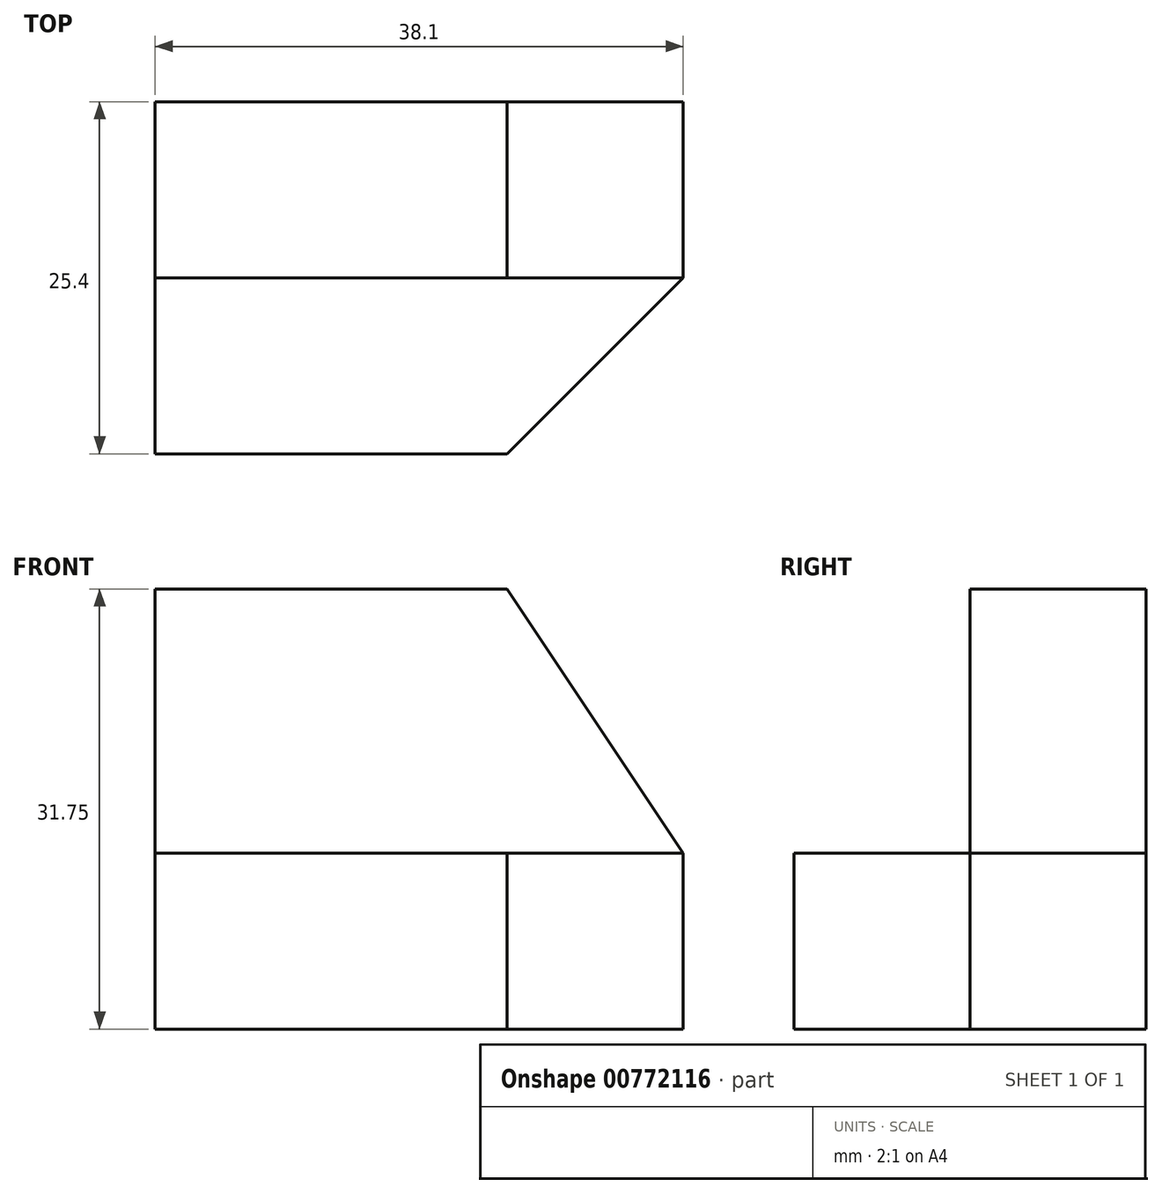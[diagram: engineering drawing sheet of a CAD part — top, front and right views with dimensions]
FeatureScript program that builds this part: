
annotation { "Feature Type Name" : "Feature", "Feature Type Description" : "" }
export const myFeature = defineFeature(function(context is Context, id is Id, definition is map)
    precondition{}
    {
        {
            var Q0;
            Q0=qCreatedBy(makeId("Right.planeOp"),FACE);
            var sketch = newSketch(context, id + "F0", { "sketchPlane" : qUnion([Q0])});
            skLineSegment(sketch, "E0", {"start": v(0, 0) * mm, "end": v(0, 31.75) * mm});
            skLineSegment(sketch, "E1", {"start": v(0, 31.75) * mm, "end": v(-12.7, 31.75) * mm});
            skLineSegment(sketch, "E2", {"start": v(-12.7, 31.75) * mm, "end": v(-12.7, 12.7) * mm});
            skLineSegment(sketch, "E3", {"start": v(-12.7, 12.7) * mm, "end": v(-25.4, 12.7) * mm});
            skLineSegment(sketch, "E4", {"start": v(-25.4, 12.7) * mm, "end": v(-25.4, 0) * mm});
            skLineSegment(sketch, "E5", {"start": v(-25.4, 0) * mm, "end": v(0, 0) * mm});
            skSolve(sketch);
        }
        {
            var Q0;
            Q0 = qSketchRegion(id + "F0", true);
            extrude(context, id + "F1", {"entities" : qUnion([Q0]), "depth" : 38.1 * mm, "offsetDistance" : 25.4 * mm});
        }
        {
            var Q0;
            Q0=makeQuery(id+"F1.opExtrude","SWEPT_FACE",FACE,{"disambiguationData":[OSD([sQuery(id+"F0.wireOp",EDGE,"E2")])]});
            var sketch = newSketch(context, id + "F2", { "sketchPlane" : qUnion([Q0])});
            skLineSegment(sketch, "E6", {"start": v(0, 31.75) * mm, "end": v(25.4, 31.75) * mm});
            skLineSegment(sketch, "E7", {"start": v(25.4, 31.75) * mm, "end": v(38.1, 12.7) * mm});
            skSolve(sketch);
        }
        {
            var Q0;
            {var subQ0=sQuery(id+"F2.wireOp",EDGE,"E7");Q0=makeQuery(id+"F2.imprint","IMPRINT",FACE,{"disambiguationData":[TD([[makeQuery(id+"F2.imprint","IMPRINT",EDGE,{"derivedFrom":subQ0}),1.0]])]});}
            extrude(context, id + "F3", {"entities" : qUnion([Q0]), "operationType" : NewBodyOperationType.REMOVE, "oppositeDirection" : true, "depth" : 12.7 * mm, "offsetDistance" : 25.4 * mm});
        }
        {
            var Q0;
            Q0=makeQuery(id+"F1.opExtrude","SWEPT_FACE",FACE,{"disambiguationData":[OSD([sQuery(id+"F0.wireOp",EDGE,"E3")])]});
            var sketch = newSketch(context, id + "F4", { "sketchPlane" : qUnion([Q0])});
            skLineSegment(sketch, "E8", {"start": v(0, -25.4) * mm, "end": v(25.4, -25.4) * mm});
            skLineSegment(sketch, "E9", {"start": v(25.4, -25.4) * mm, "end": v(38.1, -12.7) * mm});
            skSolve(sketch);
        }
        {
            var Q0;
            {var subQ0=sQuery(id+"F4.wireOp",EDGE,"E9");Q0=makeQuery(id+"F4.imprint","IMPRINT",FACE,{"disambiguationData":[TD([[makeQuery(id+"F4.imprint","IMPRINT",EDGE,{"derivedFrom":subQ0}),-1.0]])]});}
            extrude(context, id + "F5", {"entities" : qUnion([Q0]), "operationType" : NewBodyOperationType.REMOVE, "oppositeDirection" : true, "depth" : 12.7 * mm, "offsetDistance" : 25.4 * mm});
        }
    });
